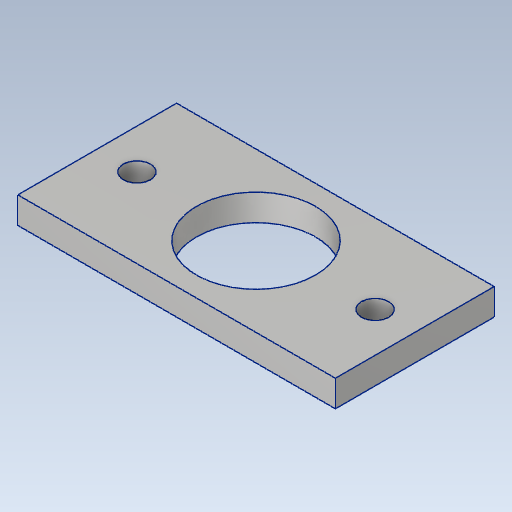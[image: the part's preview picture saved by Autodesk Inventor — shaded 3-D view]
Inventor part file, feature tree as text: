
AUTODESK INVENTOR PART (.ipt)
format: ipt  version: 2020 (Build 240168000, 168)  size: 136,704 bytes
history: native  units: in
note: dims shown in document units (in); Inventor stores cm internally (conversion verified against a paired STEP export)
features: sketch x3, other x2, hole x2, sheet_metal_op x1
ambient origin geometry x8: Origin, YZ Plane, XZ Plane, XY Plane, X Axis, Y Axis, Z Axis, Center Point
bodies: Solid1 (feature_tree)
feature tree (8):
  parser-record x1  (decoder bookkeeping rows leaked as tree rows — omitted from the tree; the rows remain in map.json)
  sheet_metal_op  "Face1"
  hole  "Hole1"  [1 undecoded]
  hole  "Hole3"  [1 undecoded]
  sketch  "Sketch1"  dims[d0=3.0in d1=1.5in]
  other  "Plate1"
  sketch  "Sketch2"  dims[d2=0.25in d3=0.75in]
  sketch  "Sketch4"  dims[d4=1.5in d5=1.125in d6=0.75in d7=0.385in d8=0.25in d9=0.5635in d10=0.25in d11=0.8108in d28=1.125in d29=1.125in d30=0.257in d31=1.0in d32=0.438in d33=0.25in d34=0.5635in d35=0.25in d36=0.8108in]
note: 2 required parameter values undecoded (feature->parameter linkage not recoverable at this tier; creation-order binding heuristic only, values carry confidence <= 0.55)
note: 1 file-system path scrubbed to <path> (originals preserved in map.json)
